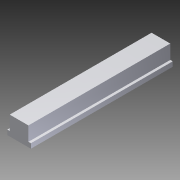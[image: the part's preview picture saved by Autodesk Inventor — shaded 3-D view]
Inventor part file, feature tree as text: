
AUTODESK INVENTOR PART (.ipt)
format: ipt  version: 2012 (Build 160160000, 160)  size: 84,992 bytes
history: native  units: in
note: dims shown in document units (in); Inventor stores cm internally (conversion verified against a paired STEP export)
features: extrude x1, sketch x1
ambient origin geometry x8: Origin, YZ Plane, XZ Plane, XY Plane, X Axis, Y Axis, Z Axis, Center Point
bodies: Solid1 (feature_tree)
feature tree (2):
  extrude  "Extrusion1"  Depth=1.0in
  sketch  "Sketch1"  dims[d0=1.25in d1=1.0in d2=0.25in d3=0.13in d4=7.5in d5=0.0in]
